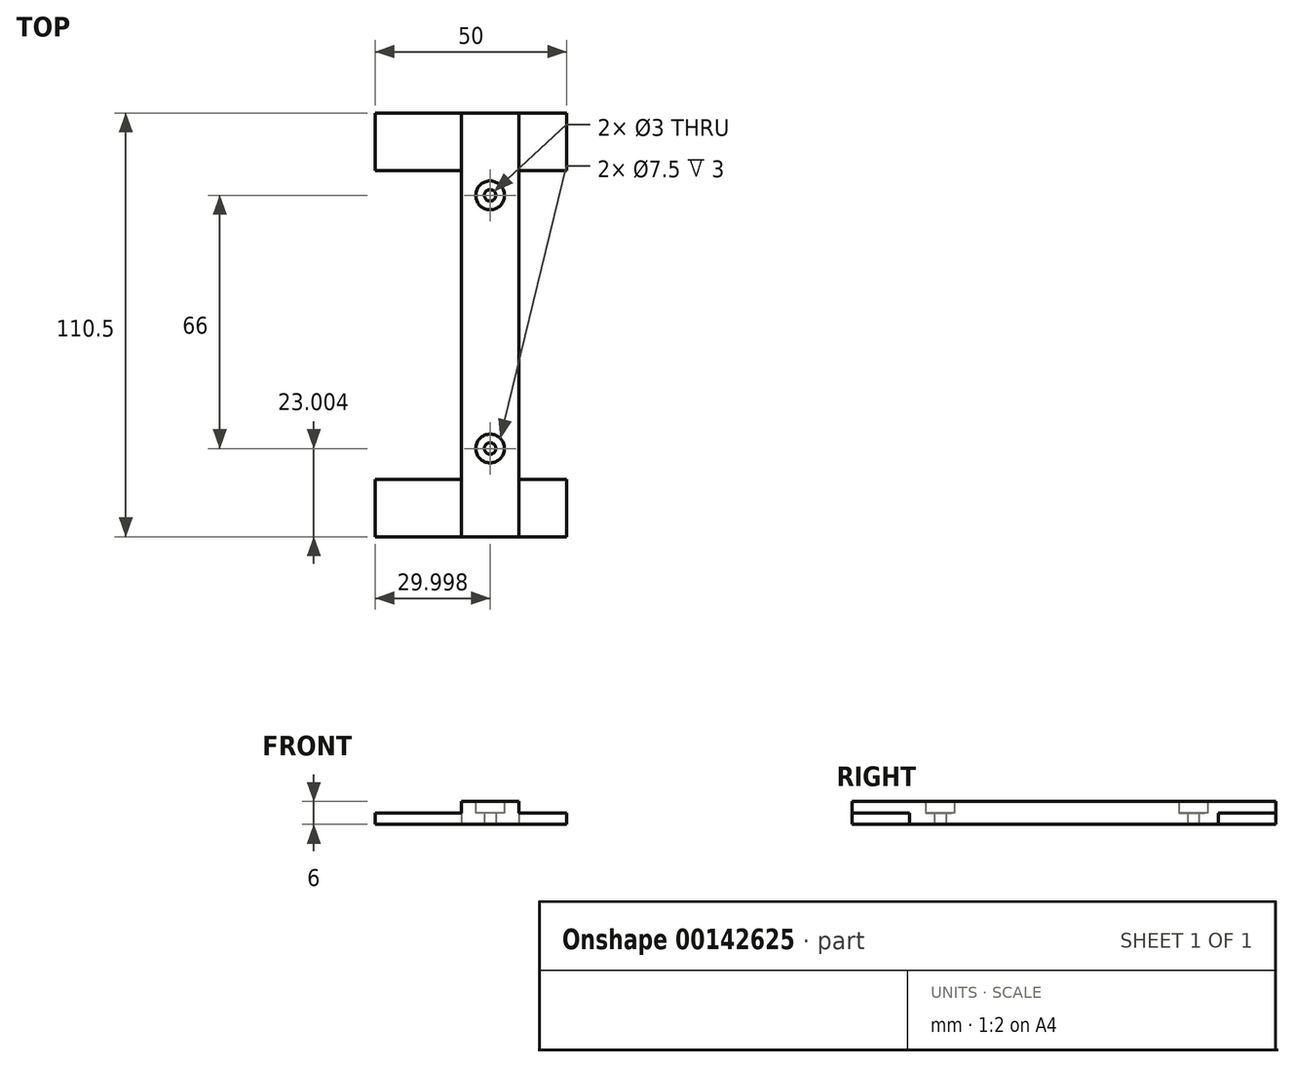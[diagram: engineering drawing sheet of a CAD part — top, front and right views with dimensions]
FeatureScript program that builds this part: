
annotation { "Feature Type Name" : "Feature", "Feature Type Description" : "" }
export const myFeature = defineFeature(function(context is Context, id is Id, definition is map)
    precondition{}
    {
        {
            var Q0;
            Q0=qCreatedBy(makeId("Top.planeOp"),FACE);
            var sketch = newSketch(context, id + "F0", { "sketchPlane" : qUnion([Q0])});
            skLineSegment(sketch, "E0", {"start": v(-55.52, 43.8) * mm, "end": v(-55.52, -22.2) * mm});
            skCircle(sketch, "E1", {"center": v(-55.52, 43.8) * mm, "radius": 1.5 * mm});
            skCircle(sketch, "E2", {"center": v(-55.52, -22.2) * mm, "radius": 1.5 * mm});
            skLineSegment(sketch, "E3", {"start": v(-55.52, 43.8) * mm, "end": v(-55.52, 65.3) * mm});
            skLineSegment(sketch, "E4", {"start": v(-55.52, -22.2) * mm, "end": v(-55.52, -45.2) * mm});
            skLineSegment(sketch, "E5", {"start": v(-55.52, 65.3) * mm, "end": v(-48.02, 65.3) * mm});
            skLineSegment(sketch, "E6", {"start": v(-48.02, 65.3) * mm, "end": v(-63.02, 65.3) * mm});
            skLineSegment(sketch, "E7.bottom", {"start": v(-63.02, 65.3) * mm, "end": v(-48.02, 65.3) * mm});
            skLineSegment(sketch, "E7.top", {"start": v(-63.02, -45.2) * mm, "end": v(-48.02, -45.2) * mm});
            skLineSegment(sketch, "E7.left", {"start": v(-63.02, 65.3) * mm, "end": v(-63.02, -45.2) * mm});
            skLineSegment(sketch, "E7.right", {"start": v(-48.02, 65.3) * mm, "end": v(-48.02, -45.2) * mm});
            skCircle(sketch, "E8", {"center": v(-55.52, -22.2) * mm, "radius": 3.75 * mm});
            skCircle(sketch, "E9", {"center": v(-55.52, 43.8) * mm, "radius": 3.75 * mm});
            skLineSegment(sketch, "E10", {"start": v(-55.52, 65.3) * mm, "end": v(-85.52, 65.3) * mm});
            skLineSegment(sketch, "E11", {"start": v(-55.52, 65.3) * mm, "end": v(-35.52, 65.3) * mm});
            skLineSegment(sketch, "E12.bottom", {"start": v(-85.52, 65.3) * mm, "end": v(-35.52, 65.3) * mm});
            skLineSegment(sketch, "E12.top", {"start": v(-85.52, 50.3) * mm, "end": v(-35.52, 50.3) * mm});
            skLineSegment(sketch, "E12.left", {"start": v(-85.52, 65.3) * mm, "end": v(-85.52, 50.3) * mm});
            skLineSegment(sketch, "E12.right", {"start": v(-35.52, 65.3) * mm, "end": v(-35.52, 50.3) * mm});
            skLineSegment(sketch, "E13", {"start": v(-55.52, -45.2) * mm, "end": v(-85.52, -45.2) * mm});
            skLineSegment(sketch, "E14", {"start": v(-55.52, -45.2) * mm, "end": v(-35.52, -45.2) * mm});
            skLineSegment(sketch, "E15.bottom", {"start": v(-35.52, -45.2) * mm, "end": v(-85.52, -45.2) * mm});
            skLineSegment(sketch, "E15.top", {"start": v(-35.52, -30.2) * mm, "end": v(-85.52, -30.2) * mm});
            skLineSegment(sketch, "E15.left", {"start": v(-35.52, -45.2) * mm, "end": v(-35.52, -30.2) * mm});
            skLineSegment(sketch, "E15.right", {"start": v(-85.52, -45.2) * mm, "end": v(-85.52, -30.2) * mm});
            skSolve(sketch);
        }
        {
            var Q0;
            {var subQ3=sQuery(id+"F0.wireOp",EDGE,"E7.left");Q0=makeQuery(id+"F0.imprint","IMPRINT",FACE,{"disambiguationData":[TD([[makeQuery(id+"F0.imprint","IMPRINT",EDGE,{"derivedFrom":subQ3}),1.0]])]});}
            var Q1;
            {var subQ5=sQuery(id+"F0.wireOp",EDGE,"E7.right");Q1=makeQuery(id+"F0.imprint","IMPRINT",FACE,{"disambiguationData":[TD([[makeQuery(id+"F0.imprint","IMPRINT",EDGE,{"derivedFrom":subQ5}),-1.0]])]});}
            var Q2;
            {var subQ0=sQuery(id+"F0.wireOp",EDGE,"E8");var subQ1=sQuery(id+"F0.wireOp",EDGE,"E0");var subQ2=makeQuery(id+"F0.imprint","INTERSECT",VERTEX,{"derivedFrom":[subQ1,subQ0]});Q2=makeQuery(id+"F0.imprint","IMPRINT",FACE,{"disambiguationData":[TD([[makeQuery(id+"F0.imprint","IMPRINT",EDGE,{"disambiguationData":[TD([[subQ2,-1.0]])],"derivedFrom":subQ1}),1.0]])]});}
            var Q3;
            {var subQ0=sQuery(id+"F0.wireOp",EDGE,"E8");var subQ1=sQuery(id+"F0.wireOp",EDGE,"E0");var subQ2=makeQuery(id+"F0.imprint","INTERSECT",VERTEX,{"derivedFrom":[subQ1,subQ0]});Q3=makeQuery(id+"F0.imprint","IMPRINT",FACE,{"disambiguationData":[TD([[makeQuery(id+"F0.imprint","IMPRINT",EDGE,{"disambiguationData":[TD([[subQ2,-1.0]])],"derivedFrom":subQ1}),-1.0]])]});}
            var Q4;
            {var subQ0=sQuery(id+"F0.wireOp",EDGE,"E1");var subQ1=sQuery(id+"F0.wireOp",EDGE,"E0");var subQ2=makeQuery(id+"F0.imprint","INTERSECT",VERTEX,{"derivedFrom":[subQ1,subQ0]});Q4=makeQuery(id+"F0.imprint","IMPRINT",FACE,{"disambiguationData":[TD([[makeQuery(id+"F0.imprint","IMPRINT",EDGE,{"disambiguationData":[TD([[subQ2,-1.0]])],"derivedFrom":subQ1}),-1.0]])]});}
            var Q5;
            {var subQ0=sQuery(id+"F0.wireOp",EDGE,"E1");var subQ1=sQuery(id+"F0.wireOp",EDGE,"E0");var subQ2=makeQuery(id+"F0.imprint","INTERSECT",VERTEX,{"derivedFrom":[subQ1,subQ0]});Q5=makeQuery(id+"F0.imprint","IMPRINT",FACE,{"disambiguationData":[TD([[makeQuery(id+"F0.imprint","IMPRINT",EDGE,{"disambiguationData":[TD([[subQ2,-1.0]])],"derivedFrom":subQ1}),1.0]])]});}
            var Q6;
            {var subQ5=sQuery(id+"F0.wireOp",EDGE,"E15.right");Q6=makeQuery(id+"F0.imprint","IMPRINT",FACE,{"disambiguationData":[TD([[makeQuery(id+"F0.imprint","IMPRINT",EDGE,{"derivedFrom":subQ5}),-1.0]])]});}
            var Q7;
            {var subQ5=sQuery(id+"F0.wireOp",EDGE,"E15.left");Q7=makeQuery(id+"F0.imprint","IMPRINT",FACE,{"disambiguationData":[TD([[makeQuery(id+"F0.imprint","IMPRINT",EDGE,{"derivedFrom":subQ5}),1.0]])]});}
            var Q8;
            {var subQ9=sQuery(id+"F0.wireOp",EDGE,"E9");var subQ10=sQuery(id+"F0.wireOp",EDGE,"E0");var subQ11=makeQuery(id+"F0.imprint","INTERSECT",VERTEX,{"derivedFrom":[subQ10,subQ9]});Q8=makeQuery(id+"F0.imprint","IMPRINT",FACE,{"disambiguationData":[TD([[makeQuery(id+"F0.imprint","IMPRINT",EDGE,{"disambiguationData":[TD([[subQ11,-1.0]])],"derivedFrom":subQ10}),1.0]])]});}
            var Q9;
            {var subQ5=sQuery(id+"F0.wireOp",EDGE,"E9");var subQ13=sQuery(id+"F0.wireOp",EDGE,"E0");var subQ14=makeQuery(id+"F0.imprint","INTERSECT",VERTEX,{"derivedFrom":[subQ13,subQ5]});Q9=makeQuery(id+"F0.imprint","IMPRINT",FACE,{"disambiguationData":[TD([[makeQuery(id+"F0.imprint","IMPRINT",EDGE,{"disambiguationData":[TD([[subQ14,-1.0]])],"derivedFrom":subQ13}),-1.0]])]});}
            var Q10;
            {var subQ5=sQuery(id+"F0.wireOp",EDGE,"E12.left");Q10=makeQuery(id+"F0.imprint","IMPRINT",FACE,{"disambiguationData":[TD([[makeQuery(id+"F0.imprint","IMPRINT",EDGE,{"derivedFrom":subQ5}),1.0]])]});}
            var Q11;
            {var subQ5=sQuery(id+"F0.wireOp",EDGE,"E12.right");Q11=makeQuery(id+"F0.imprint","IMPRINT",FACE,{"disambiguationData":[TD([[makeQuery(id+"F0.imprint","IMPRINT",EDGE,{"derivedFrom":subQ5}),-1.0]])]});}
            extrude(context, id + "F1", {"entities" : qUnion([Q0, Q1, Q2, Q3, Q4, Q5, Q6, Q7, Q8, Q9, Q10, Q11]), "depth" : 3 * mm});
        }
        {
            var Q0;
            Q0=makeQuery(id+"F1.opExtrude","CAP_FACE",FACE,{"disambiguationData":[OSD([sQuery(id+"F0.wireOp",EDGE,"E1"),sQuery(id+"F0.wireOp",EDGE,"E2"),sQuery(id+"F0.wireOp",EDGE,"E7.bottom"),sQuery(id+"F0.wireOp",EDGE,"E7.top"),sQuery(id+"F0.wireOp",EDGE,"E7.left"),sQuery(id+"F0.wireOp",EDGE,"E7.right")])],"isStart":false});
            var sketch = newSketch(context, id + "F2", { "sketchPlane" : qUnion([Q0])});
            skCircle(sketch, "E16.0", {"center": v(-55.52, -22.2) * mm, "radius": 3.75 * mm});
            skCircle(sketch, "E17.0", {"center": v(-55.52, 43.8) * mm, "radius": 3.75 * mm});
            skLineSegment(sketch, "E18.0", {"start": v(-48.02, 65.3) * mm, "end": v(-48.02, -45.2) * mm});
            skLineSegment(sketch, "E19.0", {"start": v(-63.02, 65.3) * mm, "end": v(-63.02, -45.2) * mm});
            skLineSegment(sketch, "E20.0", {"start": v(-63.02, 65.3) * mm, "end": v(-48.02, 65.3) * mm});
            skLineSegment(sketch, "E21.0", {"start": v(-63.02, -45.2) * mm, "end": v(-48.02, -45.2) * mm});
            skSolve(sketch);
        }
        {
            var Q0;
            Q0=makeQuery(id+"F2.imprint","IMPRINT",FACE,{"disambiguationData":[TD([[makeQuery(id+"F2.imprint","IMPRINT",EDGE,{"derivedFrom":sQuery(id+"F2.wireOp",EDGE,"E16.0")}),-1.0]])]});
            extrude(context, id + "F3", {"entities" : qUnion([Q0]), "operationType" : NewBodyOperationType.ADD, "depth" : 3 * mm});
        }
    });
